# Revit family: Walkway_Kattsafe_Aluminium
name_source: partatom
category: Specialty Equipment
units: mm (PartAtom-declared; Revit-internal decimal feet)

## family parameters
Cut with Voids When Loaded = No
Enable Cutting in Views = No
Maintain Annotation Orientation = No
OmniClass Number = 23.13.41.19
Part Type = Normal
Room Calculation Point = No
Round Connector Dimension = Use Diameter
Shared = No

## types (1)
- Type 1
    Assembly Code = E1090100
    Default Elevation = 0 mm  [stored 0 ft]
    Description = Kattsafe guardrail systems are the preferred method of safe access across roofs and areas close to a fall edge. The system requires no specialist PPE, personnel or training to safely prevent a fall with a walkway to designate a safe path of access across the roof surface.
    ElementType = Roof Walkway
    Export Type to IFC As = IfcBuildingElementProxy
    FrameMaterial = Aluminum_Kattsafe_Satin
    IfcExportAs = IfcBuildingElementProxy
    IfcExportType = USERDEFINED
    Manufacturer = Kattsafe®
    ManufacturerOverallHeight = 53 mm  [stored 0.173885 ft]
    ManufacturerOverallWidth = 700 mm  [stored 2.29659 ft]
    ManufacturerSpecCode = GW8
    ManufacturerURLProductSpecific = https://kattsafe.com.au
    Model = GW8
    ModifiedIssue = 20240430 $
    Type Comments = Aluminium Walkway
    Type IFC Predefined Type = USERDEFINED
    URL = https://kattsafe.com.au
    Uniclass2015Code = Pr_40_70_75_96
    Uniclass2015Title = Working platforms
    Uniclass2015Version = Products v1.23
    WalkwayMaterial = Aluminum_Kattsafe_Mesh_Walkway
    WalkwayWidth = 600 mm

note: [stored X ft] marks values corroborated as IEEE doubles in the binary element streams (Revit-internal decimal feet)

## geometry (parser evidence)
native form markers: Sweep x7
no freeform markers — native parametric forms only
